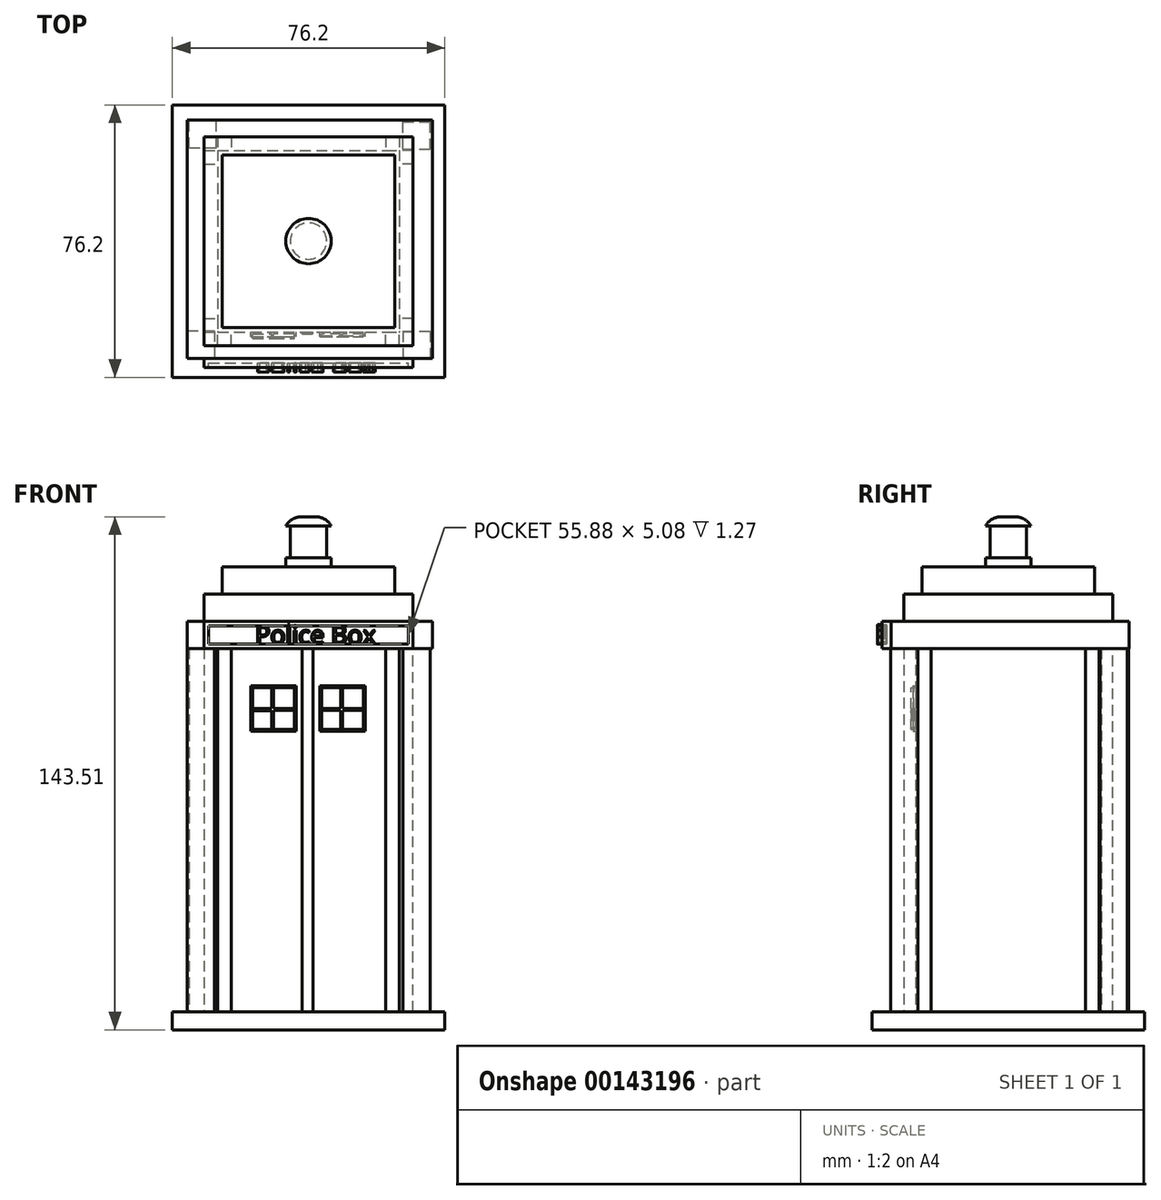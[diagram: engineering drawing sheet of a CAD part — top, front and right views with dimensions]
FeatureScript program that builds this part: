
annotation { "Feature Type Name" : "Feature", "Feature Type Description" : "" }
export const myFeature = defineFeature(function(context is Context, id is Id, definition is map)
    precondition{}
    {
        {
            var Q0;
            Q0=qCreatedBy(makeId("Front.planeOp"),FACE);
            var sketch = newSketch(context, id + "F0", { "sketchPlane" : qUnion([Q0])});
            skLineSegment(sketch, "E0.bottom", {"start": v(-38.1, 2.54) * mm, "end": v(38.1, 2.54) * mm});
            skLineSegment(sketch, "E0.top", {"start": v(-38.1, -2.54) * mm, "end": v(38.1, -2.54) * mm});
            skLineSegment(sketch, "E0.left", {"start": v(-38.1, 2.54) * mm, "end": v(-38.1, -2.54) * mm});
            skLineSegment(sketch, "E0.right", {"start": v(38.1, 2.54) * mm, "end": v(38.1, -2.54) * mm});
            skPoint(sketch, "E0.middle", {"position": v(0, 0) * mm});
            skSolve(sketch);
        }
        {
            var Q0;
            Q0=qSketchRegion(id+"F0",true);
            extrude(context, id + "F1", {"entities" : qUnion([Q0]), "depth" : 38.1 * mm, "hasSecondDirection" : true, "secondDirectionOppositeDirection" : true, "secondDirectionDepth" : 38.1 * mm});
        }
        {
            var Q0;
            Q0=makeQuery(id+"F1.opExtrude","SWEPT_FACE",FACE,{"disambiguationData":[OSD([sQuery(id+"F0.wireOp",EDGE,"E0.bottom")])]});
            var sketch = newSketch(context, id + "F2", { "sketchPlane" : qUnion([Q0])});
            skLineSegment(sketch, "E1.bottom", {"start": v(-25.4, 25.4) * mm, "end": v(25.4, 25.4) * mm});
            skLineSegment(sketch, "E1.top", {"start": v(-25.4, -25.4) * mm, "end": v(25.4, -25.4) * mm});
            skLineSegment(sketch, "E1.left", {"start": v(-25.4, 25.4) * mm, "end": v(-25.4, -25.4) * mm});
            skLineSegment(sketch, "E1.right", {"start": v(25.4, 25.4) * mm, "end": v(25.4, -25.4) * mm});
            skPoint(sketch, "E1.middle", {"position": v(0, 0) * mm});
            skSolve(sketch);
        }
        {
            var Q0;
            Q0=makeQuery(id+"F2.imprint","IMPRINT",FACE,{"disambiguationData":[TD([[makeQuery(id+"F2.imprint","IMPRINT",EDGE,{"derivedFrom":sQuery(id+"F2.wireOp",EDGE,"E1.bottom")}),-1.0]])]});
            extrude(context, id + "F3", {"entities" : qUnion([Q0]), "depth" : 101.6 * mm});
        }
        {
            var Q0;
            Q0=makeQuery(id+"F1.opExtrude","SWEPT_FACE",FACE,{"disambiguationData":[OSD([sQuery(id+"F0.wireOp",EDGE,"E0.bottom")])]});
            var sketch = newSketch(context, id + "F4", { "sketchPlane" : qUnion([Q0])});
            skLineSegment(sketch, "E2.bottom", {"start": v(-22.25, 22.42) * mm, "end": v(-31.41, 22.42) * mm});
            skLineSegment(sketch, "E2.top", {"start": v(-22.25, 31.25) * mm, "end": v(-31.41, 31.25) * mm});
            skLineSegment(sketch, "E2.left", {"start": v(-22.25, 22.42) * mm, "end": v(-22.25, 31.25) * mm});
            skLineSegment(sketch, "E2.right", {"start": v(-31.41, 22.42) * mm, "end": v(-31.41, 31.25) * mm});
            skSolve(sketch);
        }
        {
            var Q0;
            Q0=makeQuery(id+"F4.imprint","IMPRINT",FACE,{"disambiguationData":[TD([[makeQuery(id+"F4.imprint","IMPRINT",EDGE,{"derivedFrom":sQuery(id+"F4.wireOp",EDGE,"E2.bottom")}),1.0]])]});
            var sketch = newSketch(context, id + "F5", { "sketchPlane" : qUnion([Q0])});
            skLineSegment(sketch, "E3.bottom", {"start": v(-26.3, -25.15) * mm, "end": v(-33.93, -25.15) * mm});
            skLineSegment(sketch, "E3.top", {"start": v(-26.3, -32.77) * mm, "end": v(-33.93, -32.77) * mm});
            skLineSegment(sketch, "E3.left", {"start": v(-26.3, -25.15) * mm, "end": v(-26.3, -32.77) * mm});
            skLineSegment(sketch, "E3.right", {"start": v(-33.93, -25.15) * mm, "end": v(-33.93, -32.77) * mm});
            skLineSegment(sketch, "E4.bottom", {"start": v(26.41, 25.69) * mm, "end": v(34.03, 25.69) * mm});
            skLineSegment(sketch, "E4.top", {"start": v(26.41, 33.3) * mm, "end": v(34.03, 33.3) * mm});
            skLineSegment(sketch, "E4.left", {"start": v(26.41, 25.69) * mm, "end": v(26.41, 33.3) * mm});
            skLineSegment(sketch, "E4.right", {"start": v(34.03, 25.69) * mm, "end": v(34.03, 33.3) * mm});
            skLineSegment(sketch, "E5.bottom", {"start": v(26.41, -25.27) * mm, "end": v(34.03, -25.27) * mm});
            skLineSegment(sketch, "E5.top", {"start": v(26.41, -32.89) * mm, "end": v(34.03, -32.89) * mm});
            skLineSegment(sketch, "E5.left", {"start": v(26.41, -25.27) * mm, "end": v(26.41, -32.89) * mm});
            skLineSegment(sketch, "E5.right", {"start": v(34.03, -25.27) * mm, "end": v(34.03, -32.89) * mm});
            skLineSegment(sketch, "E6.bottom", {"start": v(-25.76, 26.02) * mm, "end": v(-33.38, 26.02) * mm});
            skLineSegment(sketch, "E6.top", {"start": v(-25.76, 33.64) * mm, "end": v(-33.38, 33.64) * mm});
            skLineSegment(sketch, "E6.left", {"start": v(-25.76, 26.02) * mm, "end": v(-25.76, 33.64) * mm});
            skLineSegment(sketch, "E6.right", {"start": v(-33.38, 26.02) * mm, "end": v(-33.38, 33.64) * mm});
            skSolve(sketch);
        }
        {
            var Q0;
            Q0=qSketchRegion(id+"F5",true);
            extrude(context, id + "F6", {"entities" : qUnion([Q0]), "depth" : 101.6 * mm});
        }
        {
            var Q0;
            Q0=makeQuery(id+"F3.opExtrude","SWEPT_FACE",FACE,{"disambiguationData":[OSD([sQuery(id+"F2.wireOp",EDGE,"E1.bottom")])]});
            var sketch = newSketch(context, id + "F7", { "sketchPlane" : qUnion([Q0])});
            skLineSegment(sketch, "E7.bottom", {"start": v(-25.4, 104.14) * mm, "end": v(-19.36, 104.14) * mm});
            skLineSegment(sketch, "E7.top", {"start": v(-25.4, 2.54) * mm, "end": v(-19.36, 2.54) * mm});
            skLineSegment(sketch, "E7.left", {"start": v(-25.4, 104.14) * mm, "end": v(-25.4, 2.54) * mm});
            skLineSegment(sketch, "E8.bottom", {"start": v(25.4, 104.14) * mm, "end": v(21.59, 104.14) * mm});
            skLineSegment(sketch, "E8.top", {"start": v(25.4, 2.54) * mm, "end": v(21.6, 2.54) * mm});
            skLineSegment(sketch, "E8.left", {"start": v(25.4, 104.14) * mm, "end": v(25.4, 2.54) * mm});
            skLineSegment(sketch, "E8.right", {"start": v(21.59, 104.14) * mm, "end": v(21.6, 2.54) * mm});
            skLineSegment(sketch, "E9.bottom", {"start": v(-25.4, 2.54) * mm, "end": v(-21.59, 2.54) * mm});
            skLineSegment(sketch, "E9.top", {"start": v(-25.4, 104.14) * mm, "end": v(-21.6, 104.14) * mm});
            skLineSegment(sketch, "E9.left", {"start": v(-25.4, 2.54) * mm, "end": v(-25.4, 104.14) * mm});
            skLineSegment(sketch, "E9.right", {"start": v(-21.59, 2.54) * mm, "end": v(-21.6, 104.14) * mm});
            skSolve(sketch);
        }
        {
            var Q0;
            Q0=qSketchRegion(id+"F7",true);
            extrude(context, id + "F8", {"entities" : qUnion([Q0]), "depth" : 3.8 * mm});
        }
        {
            var Q0;
            Q0=makeQuery(id+"F3.opExtrude","SWEPT_FACE",FACE,{"disambiguationData":[OSD([sQuery(id+"F2.wireOp",EDGE,"E1.right")])]});
            var sketch = newSketch(context, id + "F9", { "sketchPlane" : qUnion([Q0])});
            skLineSegment(sketch, "E10.bottom", {"start": v(-25.4, 2.54) * mm, "end": v(-21.6, 2.54) * mm});
            skLineSegment(sketch, "E10.top", {"start": v(-25.4, 104.14) * mm, "end": v(-21.6, 104.14) * mm});
            skLineSegment(sketch, "E10.left", {"start": v(-25.4, 2.54) * mm, "end": v(-25.4, 104.14) * mm});
            skLineSegment(sketch, "E10.right", {"start": v(-21.6, 2.54) * mm, "end": v(-21.6, 104.14) * mm});
            skLineSegment(sketch, "E11.bottom", {"start": v(25.4, 104.14) * mm, "end": v(21.59, 104.14) * mm});
            skLineSegment(sketch, "E11.top", {"start": v(25.4, 2.54) * mm, "end": v(21.6, 2.54) * mm});
            skLineSegment(sketch, "E11.left", {"start": v(25.4, 104.14) * mm, "end": v(25.4, 2.54) * mm});
            skLineSegment(sketch, "E11.right", {"start": v(21.59, 104.14) * mm, "end": v(21.6, 2.54) * mm});
            skSolve(sketch);
        }
        {
            var Q0;
            Q0=qSketchRegion(id+"F9",true);
            extrude(context, id + "F10", {"entities" : qUnion([Q0]), "depth" : 3.8 * mm});
        }
        {
            var Q0;
            Q0=makeQuery(id+"F3.opExtrude","SWEPT_FACE",FACE,{"disambiguationData":[OSD([sQuery(id+"F2.wireOp",EDGE,"E1.top")])]});
            var sketch = newSketch(context, id + "F11", { "sketchPlane" : qUnion([Q0])});
            skLineSegment(sketch, "E12.bottom", {"start": v(-25.4, 104.14) * mm, "end": v(-21.6, 104.14) * mm});
            skLineSegment(sketch, "E12.top", {"start": v(-25.4, 2.54) * mm, "end": v(-21.59, 2.54) * mm});
            skLineSegment(sketch, "E12.left", {"start": v(-25.4, 104.14) * mm, "end": v(-25.4, 2.54) * mm});
            skLineSegment(sketch, "E12.right", {"start": v(-21.6, 104.14) * mm, "end": v(-21.59, 2.54) * mm});
            skLineSegment(sketch, "E13.bottom", {"start": v(25.4, 104.14) * mm, "end": v(21.59, 104.14) * mm});
            skLineSegment(sketch, "E13.top", {"start": v(25.4, 2.54) * mm, "end": v(21.6, 2.54) * mm});
            skLineSegment(sketch, "E13.left", {"start": v(25.4, 104.14) * mm, "end": v(25.4, 2.54) * mm});
            skLineSegment(sketch, "E13.right", {"start": v(21.59, 104.14) * mm, "end": v(21.6, 2.54) * mm});
            skSolve(sketch);
        }
        {
            var Q0;
            Q0=qSketchRegion(id+"F11",true);
            extrude(context, id + "F12", {"entities" : qUnion([Q0]), "depth" : 3.8 * mm});
        }
        {
            var Q0;
            Q0=makeQuery(id+"F3.opExtrude","SWEPT_FACE",FACE,{"disambiguationData":[OSD([sQuery(id+"F2.wireOp",EDGE,"E1.left")])]});
            var sketch = newSketch(context, id + "F13", { "sketchPlane" : qUnion([Q0])});
            skLineSegment(sketch, "E14.bottom", {"start": v(-25.4, 104.14) * mm, "end": v(-21.59, 104.14) * mm});
            skLineSegment(sketch, "E14.top", {"start": v(-25.4, 2.54) * mm, "end": v(-21.59, 2.54) * mm});
            skLineSegment(sketch, "E14.left", {"start": v(-25.4, 104.14) * mm, "end": v(-25.4, 2.54) * mm});
            skLineSegment(sketch, "E14.right", {"start": v(-21.59, 104.14) * mm, "end": v(-21.59, 2.54) * mm});
            skLineSegment(sketch, "E15.bottom", {"start": v(25.4, 104.14) * mm, "end": v(21.59, 104.14) * mm});
            skLineSegment(sketch, "E15.top", {"start": v(25.4, 2.54) * mm, "end": v(21.6, 2.54) * mm});
            skLineSegment(sketch, "E15.left", {"start": v(25.4, 104.14) * mm, "end": v(25.4, 2.54) * mm});
            skLineSegment(sketch, "E15.right", {"start": v(21.59, 104.14) * mm, "end": v(21.6, 2.54) * mm});
            skSolve(sketch);
        }
        {
            var Q0;
            Q0=qSketchRegion(id+"F13",true);
            extrude(context, id + "F14", {"entities" : qUnion([Q0]), "depth" : 3.8 * mm});
        }
        {
            var Q0;
            Q0=makeQuery(id+"F3.opExtrude","SWEPT_FACE",FACE,{"disambiguationData":[OSD([sQuery(id+"F2.wireOp",EDGE,"E1.top")])]});
            var sketch = newSketch(context, id + "F15", { "sketchPlane" : qUnion([Q0])});
            skLineSegment(sketch, "E16.bottom", {"start": v(-16.15, 93.64) * mm, "end": v(-3.45, 93.64) * mm});
            skLineSegment(sketch, "E16.top", {"start": v(-16.15, 80.94) * mm, "end": v(-3.45, 80.94) * mm});
            skLineSegment(sketch, "E16.left", {"start": v(-16.15, 93.64) * mm, "end": v(-16.15, 80.94) * mm});
            skLineSegment(sketch, "E16.right", {"start": v(-3.45, 93.64) * mm, "end": v(-3.45, 80.94) * mm});
            skPoint(sketch, "E16.middle", {"position": v(-9.8, 87.3) * mm});
            skLineSegment(sketch, "E17.bottom", {"start": v(3.2, 93.64) * mm, "end": v(15.9, 93.64) * mm});
            skLineSegment(sketch, "E17.top", {"start": v(3.2, 80.94) * mm, "end": v(15.9, 80.94) * mm});
            skLineSegment(sketch, "E17.left", {"start": v(3.2, 93.64) * mm, "end": v(3.2, 80.94) * mm});
            skLineSegment(sketch, "E17.right", {"start": v(15.9, 93.64) * mm, "end": v(15.9, 80.94) * mm});
            skPoint(sketch, "E17.middle", {"position": v(9.55, 87.3) * mm});
            skPoint(sketch, "E17.middle.positionSnap0", {"position": v(-3.45, 87.3) * mm});
            skPoint(sketch, "E17.centerSnap0", {"position": v(-3.45, 87.3) * mm});
            skSolve(sketch);
        }
        {
            var Q0;
            Q0=qSketchRegion(id+"F15",true);
            extrude(context, id + "F16", {"entities" : qUnion([Q0]), "depth" : 1.27 * mm});
        }
        {
            var Q0;
            Q0=makeQuery(id+"F16.opExtrude","CAP_FACE",FACE,{"disambiguationData":[OSD([sQuery(id+"F15.wireOp",EDGE,"E16.bottom"),sQuery(id+"F15.wireOp",EDGE,"E16.top"),sQuery(id+"F15.wireOp",EDGE,"E16.left"),sQuery(id+"F15.wireOp",EDGE,"E16.right")])],"isStart":false});
            var Q1;
            Q1=makeQuery(id+"F16.opExtrude","CAP_FACE",FACE,{"disambiguationData":[OSD([sQuery(id+"F15.wireOp",EDGE,"E17.bottom"),sQuery(id+"F15.wireOp",EDGE,"E17.top"),sQuery(id+"F15.wireOp",EDGE,"E17.left"),sQuery(id+"F15.wireOp",EDGE,"E17.right")])],"isStart":false});
            shell(context, id + "F17", {"entities" : qUnion([Q0, Q1]), "thickness" : 0.5 * mm});
        }
        {
            var Q0;
            Q0=makeQuery(id+"F17.opShell","OFFSET_FACE",FACE,{"disambiguationData":[OSD([sQuery(id+"F15.wireOp",EDGE,"E16.bottom"),sQuery(id+"F15.wireOp",EDGE,"E16.top"),sQuery(id+"F15.wireOp",EDGE,"E16.left"),sQuery(id+"F15.wireOp",EDGE,"E16.right")])]});
            var sketch = newSketch(context, id + "F18", { "sketchPlane" : qUnion([Q0])});
            skLineSegment(sketch, "E18", {"start": v(-10.35, 93.14) * mm, "end": v(-10.35, 81.45) * mm});
            skLineSegment(sketch, "E19", {"start": v(-10.35, 81.45) * mm, "end": v(-9.8, 81.45) * mm});
            skLineSegment(sketch, "E20", {"start": v(-9.8, 81.45) * mm, "end": v(-9.8, 93.14) * mm});
            skLineSegment(sketch, "E21", {"start": v(-9.8, 93.14) * mm, "end": v(-10.35, 93.14) * mm});
            skLineSegment(sketch, "E22", {"start": v(-3.96, 87.3) * mm, "end": v(-9.8, 87.3) * mm});
            skLineSegment(sketch, "E23", {"start": v(-9.8, 87.3) * mm, "end": v(-9.8, 86.77) * mm});
            skLineSegment(sketch, "E24", {"start": v(-9.8, 86.77) * mm, "end": v(-3.96, 86.77) * mm});
            skLineSegment(sketch, "E25", {"start": v(-3.96, 86.77) * mm, "end": v(-3.96, 87.3) * mm});
            skLineSegment(sketch, "E26", {"start": v(-15.65, 87.3) * mm, "end": v(-10.35, 87.3) * mm});
            skLineSegment(sketch, "E27", {"start": v(-10.35, 87.3) * mm, "end": v(-10.35, 86.72) * mm});
            skLineSegment(sketch, "E28", {"start": v(-10.35, 86.72) * mm, "end": v(-15.65, 86.72) * mm});
            skLineSegment(sketch, "E29", {"start": v(-15.65, 86.72) * mm, "end": v(-15.65, 87.3) * mm});
            skSolve(sketch);
        }
        {
            var Q0;
            Q0=qSketchRegion(id+"F18",true);
            extrude(context, id + "F19", {"entities" : qUnion([Q0]), "operationType" : NewBodyOperationType.ADD, "depth" : 1.27 * mm});
        }
        {
            var Q0;
            Q0=makeQuery(id+"F17.opShell","OFFSET_FACE",FACE,{"disambiguationData":[OSD([sQuery(id+"F15.wireOp",EDGE,"E17.bottom"),sQuery(id+"F15.wireOp",EDGE,"E17.top"),sQuery(id+"F15.wireOp",EDGE,"E17.left"),sQuery(id+"F15.wireOp",EDGE,"E17.right")])]});
            var sketch = newSketch(context, id + "F20", { "sketchPlane" : qUnion([Q0])});
            skLineSegment(sketch, "E30", {"start": v(9.05, 93.14) * mm, "end": v(9.05, 81.45) * mm});
            skLineSegment(sketch, "E31", {"start": v(9.05, 81.45) * mm, "end": v(9.55, 81.45) * mm});
            skLineSegment(sketch, "E32", {"start": v(9.55, 81.45) * mm, "end": v(9.55, 93.14) * mm});
            skLineSegment(sketch, "E33", {"start": v(9.55, 93.14) * mm, "end": v(9.05, 93.14) * mm});
            skLineSegment(sketch, "E34", {"start": v(15.4, 87.3) * mm, "end": v(9.55, 87.3) * mm});
            skLineSegment(sketch, "E35", {"start": v(9.55, 87.3) * mm, "end": v(9.55, 86.8) * mm});
            skLineSegment(sketch, "E36", {"start": v(9.55, 86.8) * mm, "end": v(15.4, 86.8) * mm});
            skLineSegment(sketch, "E37", {"start": v(15.4, 86.8) * mm, "end": v(15.4, 87.3) * mm});
            skLineSegment(sketch, "E38", {"start": v(9.05, 87.3) * mm, "end": v(3.7, 87.3) * mm});
            skLineSegment(sketch, "E39", {"start": v(3.7, 87.3) * mm, "end": v(3.7, 86.8) * mm});
            skLineSegment(sketch, "E40", {"start": v(3.7, 86.8) * mm, "end": v(9.05, 86.8) * mm});
            skLineSegment(sketch, "E41", {"start": v(9.05, 86.8) * mm, "end": v(9.05, 87.3) * mm});
            skSolve(sketch);
        }
        {
            var Q0;
            Q0=qSketchRegion(id+"F20",true);
            extrude(context, id + "F21", {"entities" : qUnion([Q0]), "operationType" : NewBodyOperationType.ADD, "depth" : 0.5 * mm});
        }
        {
            var Q0;
            Q0=makeQuery(id+"F3.opExtrude","SWEPT_FACE",FACE,{"disambiguationData":[OSD([sQuery(id+"F2.wireOp",EDGE,"E1.top")])]});
            var sketch = newSketch(context, id + "F22", { "sketchPlane" : qUnion([Q0])});
            skLineSegment(sketch, "E42", {"start": v(-1.83, 104.14) * mm, "end": v(-1.83, 2.54) * mm});
            skLineSegment(sketch, "E43", {"start": v(-1.83, 2.54) * mm, "end": v(1.22, 2.54) * mm});
            skLineSegment(sketch, "E44", {"start": v(1.22, 2.54) * mm, "end": v(1.22, 104.14) * mm});
            skLineSegment(sketch, "E45", {"start": v(1.22, 104.14) * mm, "end": v(-1.83, 104.14) * mm});
            skSolve(sketch);
        }
        {
            var Q0;
            Q0=qSketchRegion(id+"F22",true);
            extrude(context, id + "F23", {"entities" : qUnion([Q0]), "depth" : 0.5 * mm});
        }
        {
            var Q0;
            Q0=makeQuery(id+"F6.opExtrude","CAP_FACE",FACE,{"disambiguationData":[OSD([sQuery(id+"F5.wireOp",EDGE,"E3.bottom"),sQuery(id+"F5.wireOp",EDGE,"E3.top"),sQuery(id+"F5.wireOp",EDGE,"E3.left"),sQuery(id+"F5.wireOp",EDGE,"E3.right")])],"isStart":false});
            var sketch = newSketch(context, id + "F24", { "sketchPlane" : qUnion([Q0])});
            skLineSegment(sketch, "E46.bottom", {"start": v(-33.93, -32.77) * mm, "end": v(34.65, -32.77) * mm});
            skLineSegment(sketch, "E46.top", {"start": v(-33.93, 33.88) * mm, "end": v(34.65, 33.88) * mm});
            skLineSegment(sketch, "E46.left", {"start": v(-33.93, -32.77) * mm, "end": v(-33.93, 33.88) * mm});
            skLineSegment(sketch, "E46.right", {"start": v(34.65, -32.77) * mm, "end": v(34.65, 33.88) * mm});
            skSolve(sketch);
        }
        {
            var Q0;
            Q0=qSketchRegion(id+"F24",true);
            extrude(context, id + "F25", {"entities" : qUnion([Q0]), "depth" : 7.62 * mm});
        }
        {
            var Q0;
            Q0=makeQuery(id+"F25.opExtrude","CAP_FACE",FACE,{"disambiguationData":[OSD([sQuery(id+"F24.wireOp",EDGE,"E46.bottom"),sQuery(id+"F24.wireOp",EDGE,"E46.top"),sQuery(id+"F24.wireOp",EDGE,"E46.left"),sQuery(id+"F24.wireOp",EDGE,"E46.right")])],"isStart":false});
            var sketch = newSketch(context, id + "F26", { "sketchPlane" : qUnion([Q0])});
            skLineSegment(sketch, "E47.bottom", {"start": v(-29.2, 29.21) * mm, "end": v(29.21, 29.21) * mm});
            skLineSegment(sketch, "E47.top", {"start": v(-29.21, -29.21) * mm, "end": v(29.2, -29.21) * mm});
            skLineSegment(sketch, "E47.left", {"start": v(-29.2, 29.21) * mm, "end": v(-29.21, -29.21) * mm});
            skLineSegment(sketch, "E47.right", {"start": v(29.21, 29.21) * mm, "end": v(29.2, -29.21) * mm});
            skPoint(sketch, "E47.middle", {"position": v(0, 0) * mm});
            skSolve(sketch);
        }
        {
            var Q0;
            Q0=qSketchRegion(id+"F26",true);
            extrude(context, id + "F27", {"entities" : qUnion([Q0]), "operationType" : NewBodyOperationType.ADD, "depth" : 7.62 * mm});
        }
        {
            var Q0;
            Q0=makeQuery(id+"F27.opExtrude","CAP_FACE",FACE,{"disambiguationData":[OSD([sQuery(id+"F26.wireOp",EDGE,"E47.bottom"),sQuery(id+"F26.wireOp",EDGE,"E47.top"),sQuery(id+"F26.wireOp",EDGE,"E47.left"),sQuery(id+"F26.wireOp",EDGE,"E47.right")])],"isStart":false});
            var sketch = newSketch(context, id + "F28", { "sketchPlane" : qUnion([Q0])});
            skLineSegment(sketch, "E48.bottom", {"start": v(-24.13, 24.13) * mm, "end": v(24.13, 24.13) * mm});
            skLineSegment(sketch, "E48.top", {"start": v(-24.13, -24.13) * mm, "end": v(24.13, -24.13) * mm});
            skLineSegment(sketch, "E48.left", {"start": v(-24.13, 24.13) * mm, "end": v(-24.13, -24.13) * mm});
            skLineSegment(sketch, "E48.right", {"start": v(24.13, 24.13) * mm, "end": v(24.13, -24.13) * mm});
            skPoint(sketch, "E48.middle", {"position": v(0, 0) * mm});
            skSolve(sketch);
        }
        {
            var Q0;
            Q0=qSketchRegion(id+"F28",true);
            extrude(context, id + "F29", {"entities" : qUnion([Q0]), "operationType" : NewBodyOperationType.ADD, "depth" : 7.62 * mm});
        }
        {
            var Q0;
            Q0=makeQuery(id+"F29.opExtrude","CAP_FACE",FACE,{"disambiguationData":[OSD([sQuery(id+"F28.wireOp",EDGE,"E48.bottom"),sQuery(id+"F28.wireOp",EDGE,"E48.top"),sQuery(id+"F28.wireOp",EDGE,"E48.left"),sQuery(id+"F28.wireOp",EDGE,"E48.right")])],"isStart":false});
            var sketch = newSketch(context, id + "F30", { "sketchPlane" : qUnion([Q0])});
            skCircle(sketch, "E49", {"center": v(0, 0) * mm, "radius": 6.35 * mm});
            skSolve(sketch);
        }
        {
            var Q0;
            Q0=qSketchRegion(id+"F30",true);
            extrude(context, id + "F31", {"entities" : qUnion([Q0]), "operationType" : NewBodyOperationType.ADD, "depth" : 2.54 * mm});
        }
        {
            var Q0;
            Q0=makeQuery(id+"F31.opExtrude","CAP_FACE",FACE,{"disambiguationData":[OSD([sQuery(id+"F30.wireOp",EDGE,"E49")])],"isStart":false});
            var sketch = newSketch(context, id + "F32", { "sketchPlane" : qUnion([Q0])});
            skCircle(sketch, "E50", {"center": v(0, 0) * mm, "radius": 5.08 * mm});
            skSolve(sketch);
        }
        {
            var Q0;
            Q0=qSketchRegion(id+"F32",true);
            extrude(context, id + "F33", {"entities" : qUnion([Q0]), "depth" : 8.9 * mm});
        }
        {
            var Q0;
            Q0=makeQuery(id+"F33.opExtrude","CAP_FACE",FACE,{"disambiguationData":[OSD([sQuery(id+"F32.wireOp",EDGE,"E50")])],"isStart":false});
            var sketch = newSketch(context, id + "F34", { "sketchPlane" : qUnion([Q0])});
            skCircle(sketch, "E51", {"center": v(0, 0) * mm, "radius": 6.35 * mm});
            skSolve(sketch);
        }
        {
            var Q0;
            Q0=qSketchRegion(id+"F34",true);
            extrude(context, id + "F35", {"entities" : qUnion([Q0]), "depth" : 2.54 * mm});
        }
        {
            var Q0;
            Q0=makeQuery(id+"F35.opExtrude","CAP_EDGE",EDGE,{"disambiguationData":[OSD([sQuery(id+"F34.wireOp",EDGE,"E51")])],"isStart":false});
            fillet(context, id + "F36", {"entities" : qUnion([Q0]), "radius" : 5.08 * mm, "tangentPropagation" : true, "allowEdgeOverflow" : false});
        }
        {
            var Q0;
            Q0=makeQuery(id+"F25.opExtrude","SWEPT_FACE",FACE,{"disambiguationData":[OSD([sQuery(id+"F24.wireOp",EDGE,"E46.bottom")])]});
            var sketch = newSketch(context, id + "F37", { "sketchPlane" : qUnion([Q0])});
            skLineSegment(sketch, "E52.bottom", {"start": v(-29.21, 111.76) * mm, "end": v(29.21, 111.76) * mm});
            skLineSegment(sketch, "E52.top", {"start": v(-29.21, 104.14) * mm, "end": v(29.21, 104.14) * mm});
            skLineSegment(sketch, "E52.left", {"start": v(-29.21, 111.76) * mm, "end": v(-29.21, 104.14) * mm});
            skLineSegment(sketch, "E52.right", {"start": v(29.21, 111.76) * mm, "end": v(29.21, 104.14) * mm});
            skPoint(sketch, "E52.middle", {"position": v(0, 107.95) * mm});
            skSolve(sketch);
        }
        {
            var Q0;
            Q0=qSketchRegion(id+"F37",true);
            extrude(context, id + "F38", {"entities" : qUnion([Q0]), "depth" : 2.54 * mm});
        }
        {
            var Q0;
            Q0=makeQuery(id+"F38.opExtrude","CAP_FACE",FACE,{"disambiguationData":[OSD([sQuery(id+"F37.wireOp",EDGE,"E52.bottom"),sQuery(id+"F37.wireOp",EDGE,"E52.top"),sQuery(id+"F37.wireOp",EDGE,"E52.left"),sQuery(id+"F37.wireOp",EDGE,"E52.right")])],"isStart":false});
            shell(context, id + "F39", {"entities" : qUnion([Q0]), "thickness" : 1.27 * mm});
        }
        {
            var Q0;
            Q0=makeQuery(id+"F39.opShell","OFFSET_FACE",FACE,{"disambiguationData":[OSD([sQuery(id+"F37.wireOp",EDGE,"E52.bottom"),sQuery(id+"F37.wireOp",EDGE,"E52.top"),sQuery(id+"F37.wireOp",EDGE,"E52.left"),sQuery(id+"F37.wireOp",EDGE,"E52.right")])]});
            var sketch = newSketch(context, id + "F40", { "sketchPlane" : qUnion([Q0])});
            skText(sketch, "E53", { "text": "Police Box", "fontName": "OpenSans-Regular.ttf"});
            const initialGuessF40  = {"E53": [-0.01495, 0.10541, 1, 0, 0.00508]};
            skSetInitialGuess(sketch, initialGuessF40);
            skSolve(sketch);
        }
        {
            var Q0;
            Q0=qSketchRegion(id+"F40",true);
            extrude(context, id + "F41", {"entities" : qUnion([Q0]), "depth" : 2.54 * mm});
        }
    });
